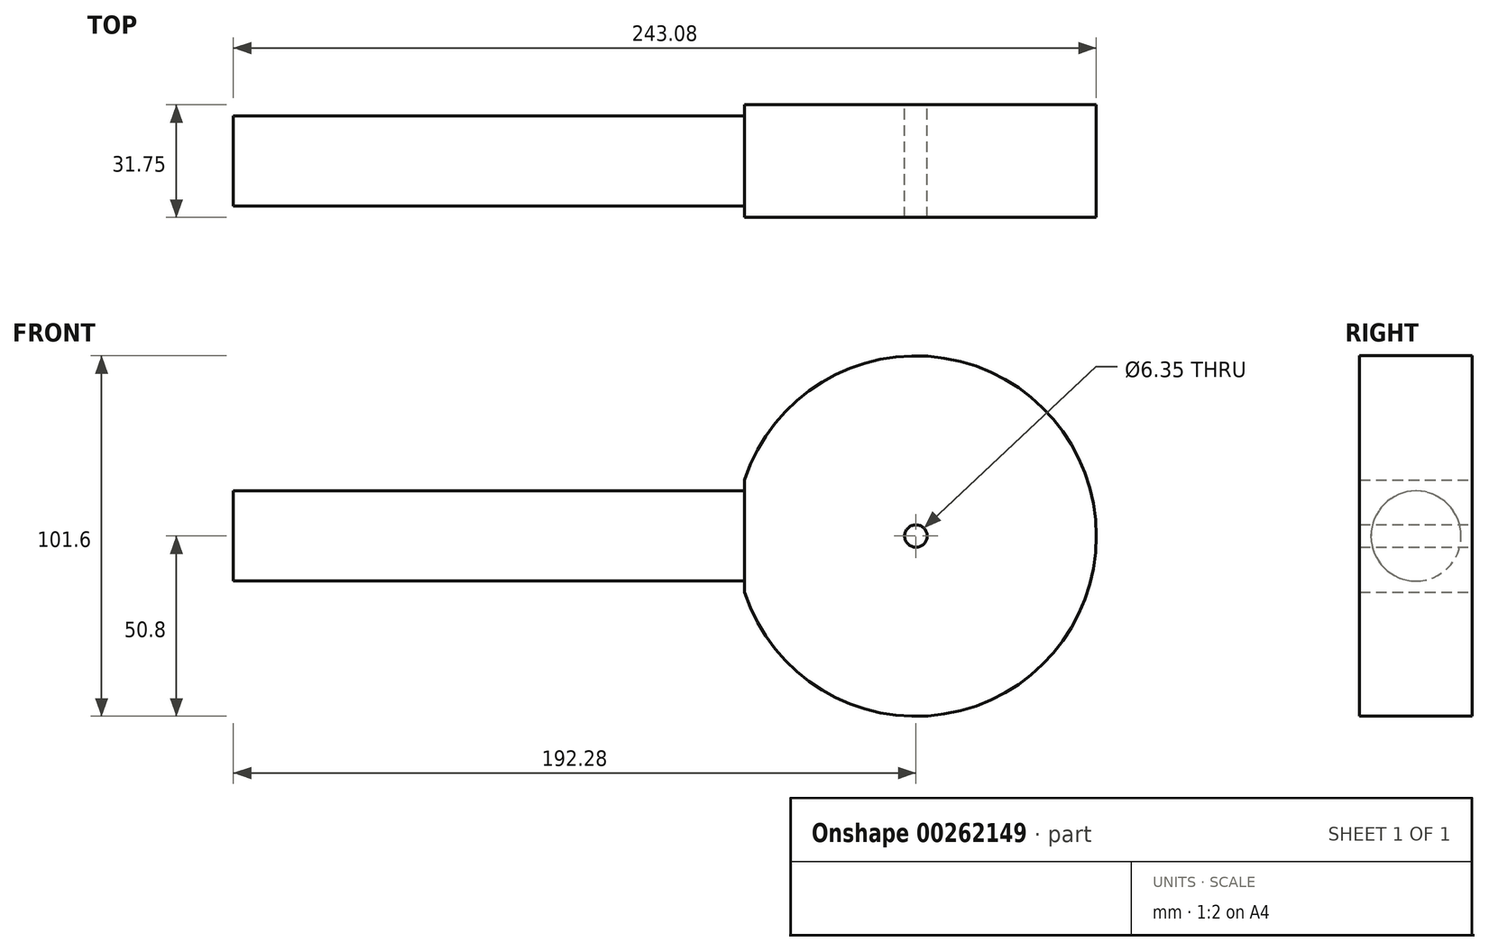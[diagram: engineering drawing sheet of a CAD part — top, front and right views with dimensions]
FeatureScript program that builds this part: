
annotation { "Feature Type Name" : "Feature", "Feature Type Description" : "" }
export const myFeature = defineFeature(function(context is Context, id is Id, definition is map)
    precondition{}
    {
        {
            var Q0;
            Q0=qCreatedBy(makeId("Front.planeOp"),FACE);
            var sketch = newSketch(context, id + "F0", { "sketchPlane" : qUnion([Q0])});
            skCircle(sketch, "E0", {"center": v(0, 0) * mm, "radius": 50.8 * mm});
            skLineSegment(sketch, "E1", {"start": v(-48.26, 53.65) * mm, "end": v(-48.26, -57.76) * mm, "construction": true});
            skLineSegment(sketch, "E2", {"start": v(-48.26, 15.86) * mm, "end": v(-48.26, -15.86) * mm});
            skCircle(sketch, "E3", {"center": v(0, 0) * mm, "radius": 3.18 * mm});
            skSolve(sketch);
        }
        {
            var Q0;
            {var subQ0=sQuery(id+"F0.wireOp",EDGE,"E2");Q0=makeQuery(id+"F0.imprint","IMPRINT",FACE,{"disambiguationData":[TD([[makeQuery(id+"F0.imprint","IMPRINT",EDGE,{"derivedFrom":subQ0}),1.0]])]});}
            extrude(context, id + "F1", {"entities" : qUnion([Q0]), "depth" : 31.75 * mm});
        }
        {
            var Q0;
            Q0=makeQuery(id+"F1.opExtrude","SWEPT_FACE",FACE,{"disambiguationData":[OSD([sQuery(id+"F0.wireOp",EDGE,"E2")])]});
            var sketch = newSketch(context, id + "F2", { "sketchPlane" : qUnion([Q0])});
            skCircle(sketch, "E4", {"center": v(15.88, 0) * mm, "radius": 12.7 * mm});
            skPoint(sketch, "E4.centerSnap0", {"position": v(15.88, 15.86) * mm});
            skPoint(sketch, "E4.centerSnap1", {"position": v(31.75, 0) * mm});
            skSolve(sketch);
        }
        {
            var Q0;
            Q0=makeQuery(id+"F2.imprint","IMPRINT",FACE,{"disambiguationData":[TD([[makeQuery(id+"F2.imprint","IMPRINT",EDGE,{"derivedFrom":sQuery(id+"F2.wireOp",EDGE,"E4")}),1.0]])]});
            extrude(context, id + "F3", {"entities" : qUnion([Q0]), "operationType" : NewBodyOperationType.ADD, "depth" : 144.02 * mm});
        }
    });
